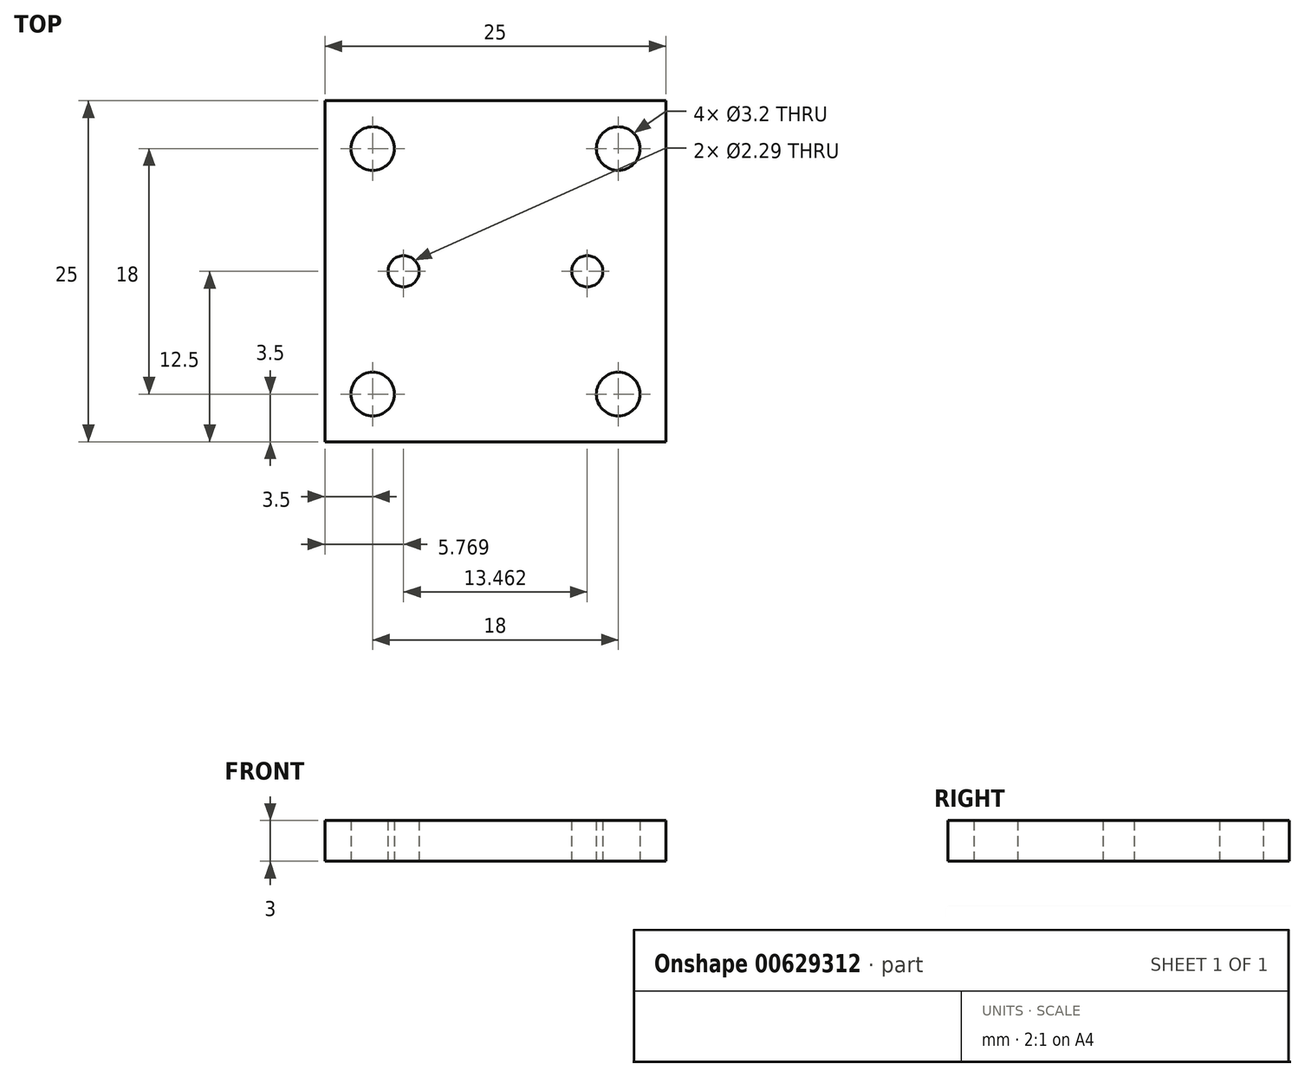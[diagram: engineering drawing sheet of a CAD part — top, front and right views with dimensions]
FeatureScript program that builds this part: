
annotation { "Feature Type Name" : "Feature", "Feature Type Description" : "" }
export const myFeature = defineFeature(function(context is Context, id is Id, definition is map)
    precondition{}
    {
        {
            var Q0;
            Q0=qCreatedBy(makeId("Top.planeOp"),FACE);
            var sketch = newSketch(context, id + "F0", { "sketchPlane" : qUnion([Q0])});
            skPoint(sketch, "E0", {"position": v(-6.73, 0) * mm});
            skPoint(sketch, "E1", {"position": v(6.73, 0) * mm});
            skLineSegment(sketch, "E2.bottom", {"start": v(12.5, -12.5) * mm, "end": v(-12.5, -12.5) * mm});
            skLineSegment(sketch, "E2.top", {"start": v(12.5, 12.5) * mm, "end": v(-12.5, 12.5) * mm});
            skLineSegment(sketch, "E2.left", {"start": v(12.5, -12.5) * mm, "end": v(12.5, 12.5) * mm});
            skLineSegment(sketch, "E2.right", {"start": v(-12.5, -12.5) * mm, "end": v(-12.5, 12.5) * mm});
            skPoint(sketch, "E2.middle", {"position": v(0, 0) * mm});
            skLineSegment(sketch, "E3.bottom", {"start": v(9, -9) * mm, "end": v(-9, -9) * mm, "construction": true});
            skLineSegment(sketch, "E3.top", {"start": v(9, 9) * mm, "end": v(-9, 9) * mm, "construction": true});
            skLineSegment(sketch, "E3.left", {"start": v(9, -9) * mm, "end": v(9, 9) * mm, "construction": true});
            skLineSegment(sketch, "E3.right", {"start": v(-9, -9) * mm, "end": v(-9, 9) * mm, "construction": true});
            skCircle(sketch, "E4", {"center": v(0, 0) * mm, "radius": 6 * mm, "construction": true});
            skSolve(sketch);
        }
        {
            var Q0;
            Q0=makeQuery(id+"F0.imprint","IMPRINT",FACE,{"disambiguationData":[TD([[makeQuery(id+"F0.imprint","IMPRINT",EDGE,{"derivedFrom":sQuery(id+"F0.wireOp",EDGE,"E2.bottom")}),-1.0]])]});
            extrude(context, id + "F1", {"entities" : qUnion([Q0]), "depth" : 3 * mm, "offsetDistance" : 25 * mm});
        }
        {
            var Q0;
            Q0=sQuery(id+"F0.wireOp",VERTEX,"E0");
            var Q1;
            Q1=sQuery(id+"F0.wireOp",VERTEX,"E1");
            var Q2;
            Q2=makeQuery(id+"F1.opExtrude","SWEPT_BODY",BODY,{"disambiguationData":[OSD([sQuery(id+"F0.wireOp",EDGE,"E2.bottom"),sQuery(id+"F0.wireOp",EDGE,"E2.top"),sQuery(id+"F0.wireOp",EDGE,"E2.left"),sQuery(id+"F0.wireOp",EDGE,"E2.right")])]});
            hole(context, id + "F2", {"style" : HoleStyle.SIMPLE, "endStyle" : HoleEndStyle.THROUGH, "oppositeDirection" : true, "holeDiameter" : 2.3 * mm, "majorDiameter" : 5 * mm, "isTappedThrough" : true, "tappedDepth" : 2.3 * mm, "tapClearance" : 3, "startFromSketch" : true, "locations" : qUnion([Q0, Q1]), "scope" : qUnion([Q2])});
        }
        {
            var Q0;
            Q0=sQuery(id+"F0.wireOp",VERTEX,"E3.right.end");
            var Q1;
            Q1=sQuery(id+"F0.wireOp",VERTEX,"E3.right.start");
            var Q2;
            Q2=sQuery(id+"F0.wireOp",VERTEX,"E3.top.start");
            var Q3;
            Q3=sQuery(id+"F0.wireOp",VERTEX,"E3.left.start");
            var Q4;
            Q4=makeQuery(id+"F1.opExtrude","SWEPT_BODY",BODY,{"disambiguationData":[OSD([sQuery(id+"F0.wireOp",EDGE,"E2.bottom"),sQuery(id+"F0.wireOp",EDGE,"E2.top"),sQuery(id+"F0.wireOp",EDGE,"E2.left"),sQuery(id+"F0.wireOp",EDGE,"E2.right")])]});
            hole(context, id + "F3", {"style" : HoleStyle.SIMPLE, "endStyle" : HoleEndStyle.THROUGH, "oppositeDirection" : true, "holeDiameter" : 3.2 * mm, "majorDiameter" : 5 * mm, "isTappedThrough" : true, "tappedDepth" : 2.3 * mm, "tapClearance" : 3, "startFromSketch" : true, "locations" : qUnion([Q0, Q1, Q2, Q3]), "scope" : qUnion([Q4])});
        }
    });
